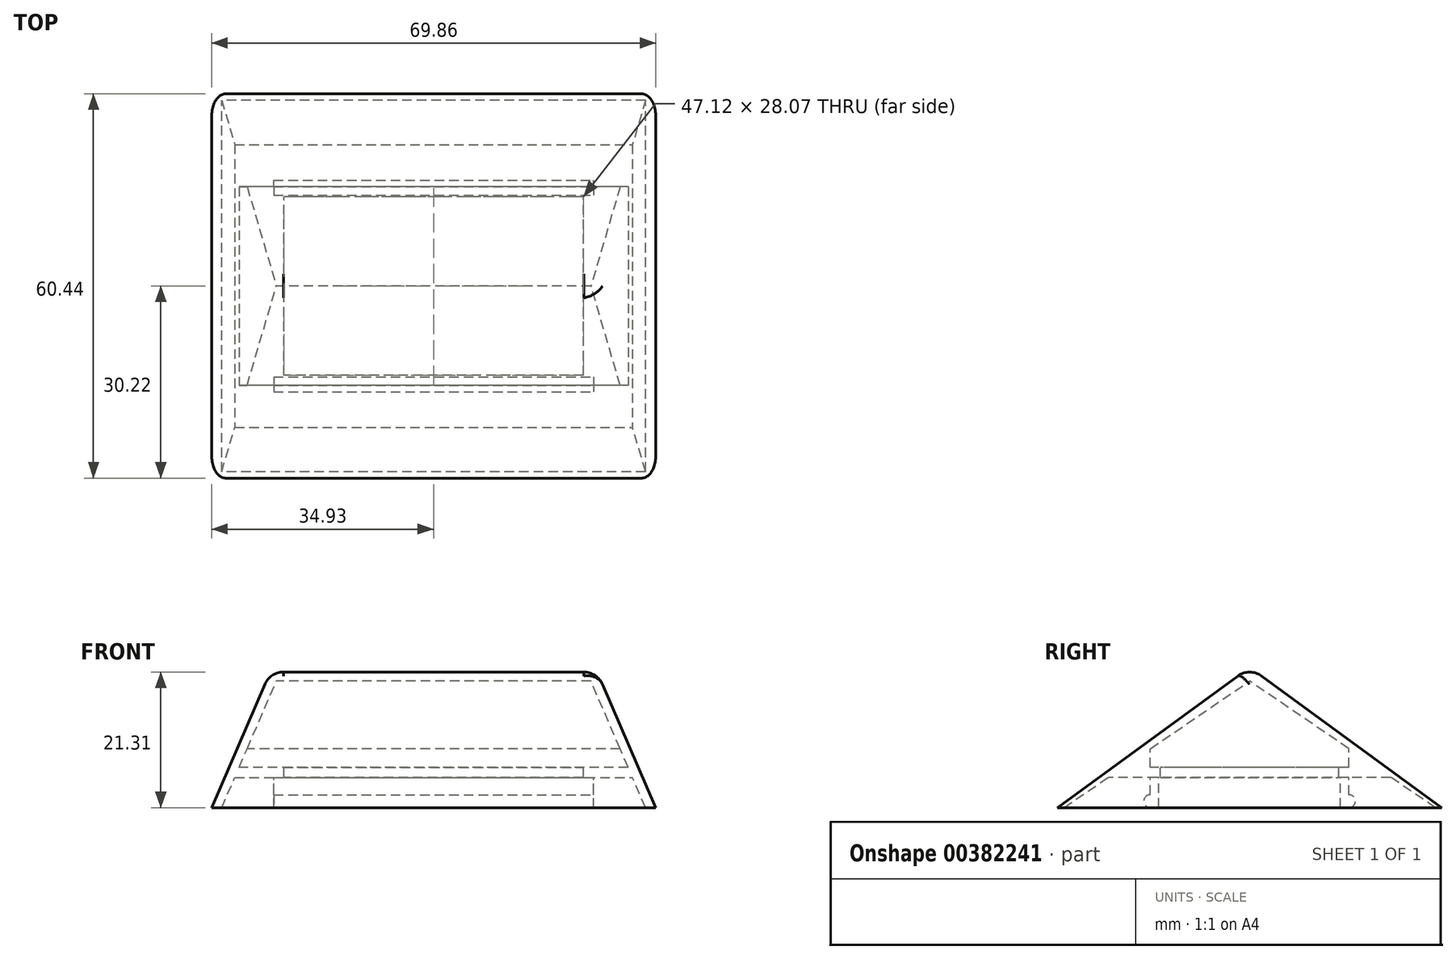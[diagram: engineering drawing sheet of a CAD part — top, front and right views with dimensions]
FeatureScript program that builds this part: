
annotation { "Feature Type Name" : "Feature", "Feature Type Description" : "" }
export const myFeature = defineFeature(function(context is Context, id is Id, definition is map)
    precondition{}
    {
        {
            var Q0;
            Q0=qCreatedBy(makeId("Top.planeOp"),FACE);
            var sketch = newSketch(context, id + "F0", { "sketchPlane" : qUnion([Q0])});
            skLineSegment(sketch, "E0.bottom", {"start": v(-31.75, 22.22) * mm, "end": v(31.75, 22.22) * mm});
            skLineSegment(sketch, "E0.top", {"start": v(-31.75, -22.22) * mm, "end": v(31.75, -22.22) * mm});
            skLineSegment(sketch, "E0.left", {"start": v(-31.75, 22.23) * mm, "end": v(-31.75, -22.22) * mm});
            skLineSegment(sketch, "E0.right", {"start": v(31.75, 22.23) * mm, "end": v(31.75, -22.22) * mm});
            skLineSegment(sketch, "E1.0", {"start": v(-25.15, 15.62) * mm, "end": v(25.15, 15.62) * mm});
            skLineSegment(sketch, "E1.1", {"start": v(-25.15, 15.62) * mm, "end": v(-25.15, -15.62) * mm});
            skLineSegment(sketch, "E1.2", {"start": v(-25.15, -15.62) * mm, "end": v(25.15, -15.62) * mm});
            skLineSegment(sketch, "E1.3", {"start": v(25.15, 15.62) * mm, "end": v(25.15, -15.62) * mm});
            skLineSegment(sketch, "E2", {"start": v(-25.15, 15.62) * mm, "end": v(25.15, -15.62) * mm, "construction": true});
            skLineSegment(sketch, "E3", {"start": v(25.15, 15.62) * mm, "end": v(-25.15, -15.62) * mm, "construction": true});
            skSolve(sketch);
        }
        {
            var Q0;
            Q0 = qSketchRegion(id + "F0", true);
            extrude(context, id + "F1", {"entities" : qUnion([Q0]), "depth" : 1.59 * mm});
        }
        {
            var Q0;
            Q0=makeQuery(id+"F1.opExtrude","CAP_FACE",FACE,{"disambiguationData":[OSD([sQuery(id+"F0.wireOp",EDGE,"E0.bottom"),sQuery(id+"F0.wireOp",EDGE,"E0.top"),sQuery(id+"F0.wireOp",EDGE,"E0.left"),sQuery(id+"F0.wireOp",EDGE,"E0.right"),sQuery(id+"F0.wireOp",EDGE,"E1.0"),sQuery(id+"F0.wireOp",EDGE,"E1.1"),sQuery(id+"F0.wireOp",EDGE,"E1.2"),sQuery(id+"F0.wireOp",EDGE,"E1.3")])],"isStart":false});
            var sketch = newSketch(context, id + "F2", { "sketchPlane" : qUnion([Q0])});
            skLineSegment(sketch, "E4.bottom", {"start": v(-25.15, 15.62) * mm, "end": v(25.15, 15.62) * mm});
            skLineSegment(sketch, "E4.top", {"start": v(-25.15, -15.62) * mm, "end": v(25.15, -15.62) * mm});
            skLineSegment(sketch, "E4.left", {"start": v(-25.15, 15.62) * mm, "end": v(-25.15, -15.62) * mm});
            skLineSegment(sketch, "E4.right", {"start": v(25.15, 15.62) * mm, "end": v(25.15, -15.62) * mm});
            skLineSegment(sketch, "E5.0", {"start": v(-23.56, 14.03) * mm, "end": v(23.56, 14.03) * mm});
            skLineSegment(sketch, "E5.1", {"start": v(-23.56, 14.03) * mm, "end": v(-23.56, -14.03) * mm});
            skLineSegment(sketch, "E5.2", {"start": v(-23.56, -14.03) * mm, "end": v(23.56, -14.03) * mm});
            skLineSegment(sketch, "E5.3", {"start": v(23.56, 14.03) * mm, "end": v(23.56, -14.03) * mm});
            skSolve(sketch);
        }
        {
            var Q0;
            Q0 = qSketchRegion(id + "F2", true);
            extrude(context, id + "F3", {"entities" : qUnion([Q0]), "operationType" : NewBodyOperationType.ADD, "oppositeDirection" : true, "depth" : 6.35 * mm});
        }
        {
            var Q0;
            Q0=qCreatedBy(makeId("Right.planeOp"),FACE);
            var sketch = newSketch(context, id + "F4", { "sketchPlane" : qUnion([Q0])});
            skLineSegment(sketch, "E6", {"start": v(0, 15.15) * mm, "end": v(15.61, 4.5) * mm});
            skLineSegment(sketch, "E7", {"start": v(29.21, -4.76) * mm, "end": v(32.39, -4.76) * mm});
            skLineSegment(sketch, "E8", {"start": v(32.39, -4.76) * mm, "end": v(0, 17.3) * mm});
            skLineSegment(sketch, "E9", {"start": v(15.61, 4.5) * mm, "end": v(15.61, 0) * mm});
            skLineSegment(sketch, "E10", {"start": v(15.61, 0) * mm, "end": v(22.23, 0) * mm});
            skLineSegment(sketch, "E11.trimOffspring", {"start": v(22.23, 0) * mm, "end": v(29.21, -4.76) * mm});
            skLineSegment(sketch, "E12.MirrorCS", {"start": v(0, 15.15) * mm, "end": v(-15.61, 4.5) * mm});
            skLineSegment(sketch, "E13.MirrorCS", {"start": v(-32.39, -4.76) * mm, "end": v(0, 17.3) * mm});
            skLineSegment(sketch, "E14.MirrorCS", {"start": v(-15.61, 4.5) * mm, "end": v(-15.61, 0) * mm});
            skLineSegment(sketch, "E15.MirrorCS", {"start": v(-29.21, -4.76) * mm, "end": v(-32.39, -4.76) * mm});
            skLineSegment(sketch, "E16.MirrorCS", {"start": v(-15.61, 0) * mm, "end": v(-22.23, 0) * mm});
            skLineSegment(sketch, "E17.MirrorCS", {"start": v(-22.23, 0) * mm, "end": v(-29.21, -4.76) * mm});
            skSolve(sketch);
        }
        {
            var Q0;
            Q0 = qSketchRegion(id + "F4", true);
            extrude(context, id + "F5", {"entities" : qUnion([Q0]), "operationType" : NewBodyOperationType.ADD, "endBound" : BoundingType.SYMMETRIC, "depth" : 69.85 * mm});
        }
        {
            var Q0;
            Q0=qCreatedBy(makeId("Front.planeOp"),FACE);
            var sketch = newSketch(context, id + "F6", { "sketchPlane" : qUnion([Q0])});
            skLineSegment(sketch, "E18", {"start": v(-25.4, 17.3) * mm, "end": v(-34.93, -4.76) * mm});
            skLineSegment(sketch, "E19", {"start": v(-25.4, 17.3) * mm, "end": v(-34.93, 17.3) * mm});
            skLineSegment(sketch, "E20", {"start": v(-34.93, 17.3) * mm, "end": v(-34.93, -4.76) * mm});
            skLineSegment(sketch, "E21.MirrorCS", {"start": v(34.93, 17.3) * mm, "end": v(34.93, -4.76) * mm});
            skLineSegment(sketch, "E22.MirrorCS", {"start": v(25.4, 17.3) * mm, "end": v(34.93, 17.3) * mm});
            skLineSegment(sketch, "E23.MirrorCS", {"start": v(25.4, 17.3) * mm, "end": v(34.93, -4.76) * mm});
            skSolve(sketch);
        }
        {
            var Q0;
            Q0 = qSketchRegion(id + "F6", true);
            extrude(context, id + "F7", {"entities" : qUnion([Q0]), "operationType" : NewBodyOperationType.REMOVE, "endBound" : BoundingType.SYMMETRIC, "oppositeDirection" : true, "depth" : 76.2 * mm});
        }
        {
            var Q0;
            Q0=qCreatedBy(makeId("Front.planeOp"),FACE);
            var sketch = newSketch(context, id + "F8", { "sketchPlane" : qUnion([Q0])});
            skLineSegment(sketch, "E24", {"start": v(-25.4, 17.3) * mm, "end": v(-34.93, -4.76) * mm});
            skLineSegment(sketch, "E25", {"start": v(-34.93, -4.76) * mm, "end": v(-33.34, -4.76) * mm});
            skLineSegment(sketch, "E26", {"start": v(-33.34, -4.76) * mm, "end": v(-23.81, 17.3) * mm});
            skLineSegment(sketch, "E27", {"start": v(-23.81, 17.3) * mm, "end": v(-25.4, 17.3) * mm});
            skLineSegment(sketch, "E28.MirrorCS", {"start": v(25.4, 17.3) * mm, "end": v(34.93, -4.76) * mm});
            skLineSegment(sketch, "E29.MirrorCS", {"start": v(23.81, 17.3) * mm, "end": v(25.4, 17.3) * mm});
            skLineSegment(sketch, "E30.MirrorCS", {"start": v(34.93, -4.76) * mm, "end": v(33.34, -4.76) * mm});
            skLineSegment(sketch, "E31.MirrorCS", {"start": v(33.34, -4.76) * mm, "end": v(23.81, 17.3) * mm});
            skSolve(sketch);
        }
        {
            var Q0;
            Q0 = qSketchRegion(id + "F8", true);
            extrude(context, id + "F9", {"entities" : qUnion([Q0]), "operationType" : NewBodyOperationType.ADD, "endBound" : BoundingType.SYMMETRIC, "depth" : 76.2 * mm});
        }
        {
            var Q0;
            Q0=qCreatedBy(makeId("Right.planeOp"),FACE);
            var sketch = newSketch(context, id + "F10", { "sketchPlane" : qUnion([Q0])});
            skLineSegment(sketch, "E32", {"start": v(0, 17.3) * mm, "end": v(-30.22, -4.76) * mm});
            skLineSegment(sketch, "E33", {"start": v(-30.22, -4.76) * mm, "end": v(-38.1, -4.76) * mm});
            skLineSegment(sketch, "E34", {"start": v(-38.1, -4.76) * mm, "end": v(-38.1, 17.3) * mm});
            skLineSegment(sketch, "E35", {"start": v(-38.1, 17.3) * mm, "end": v(0, 17.3) * mm});
            skLineSegment(sketch, "E36.MirrorCS", {"start": v(0, 17.3) * mm, "end": v(30.22, -4.76) * mm});
            skLineSegment(sketch, "E37.MirrorCS", {"start": v(30.22, -4.76) * mm, "end": v(38.1, -4.76) * mm});
            skLineSegment(sketch, "E38.MirrorCS", {"start": v(38.1, -4.76) * mm, "end": v(38.1, 17.3) * mm});
            skLineSegment(sketch, "E39.MirrorCS", {"start": v(38.1, 17.3) * mm, "end": v(0, 17.3) * mm});
            skSolve(sketch);
        }
        {
            var Q0;
            Q0 = qSketchRegion(id + "F10", true);
            extrude(context, id + "F11", {"entities" : qUnion([Q0]), "operationType" : NewBodyOperationType.REMOVE, "endBound" : BoundingType.SYMMETRIC, "oppositeDirection" : true, "depth" : 76.2 * mm});
        }
        {
            var Q0;
            Q0=makeQuery(id+"F11.boolean.opBoolean","INTERSECT",EDGE,{"derivedFrom":[makeQuery(id+"F9.boolean.opBoolean","MERGE",FACE,{"derivedFrom":[makeQuery(id+"F7.boolean.opBoolean","COPY",FACE,{"derivedFrom":makeQuery(id+"F7.opExtrude","SWEPT_FACE",FACE,{"disambiguationData":[OSD([sQuery(id+"F6.wireOp",EDGE,"E23.MirrorCS")])]})}),makeQuery(id+"F9.opExtrude","SWEPT_FACE",FACE,{"disambiguationData":[OSD([sQuery(id+"F8.wireOp",EDGE,"E28.MirrorCS")])]})]}),makeQuery(id+"F11.opExtrude","SWEPT_FACE",FACE,{"disambiguationData":[OSD([sQuery(id+"F10.wireOp",EDGE,"E32")])]})]});
            var Q1;
            Q1=makeQuery(id+"F11.boolean.opBoolean","INTERSECT",EDGE,{"derivedFrom":[makeQuery(id+"F9.boolean.opBoolean","MERGE",FACE,{"derivedFrom":[makeQuery(id+"F7.boolean.opBoolean","COPY",FACE,{"derivedFrom":makeQuery(id+"F7.opExtrude","SWEPT_FACE",FACE,{"disambiguationData":[OSD([sQuery(id+"F6.wireOp",EDGE,"E23.MirrorCS")])]})}),makeQuery(id+"F9.opExtrude","SWEPT_FACE",FACE,{"disambiguationData":[OSD([sQuery(id+"F8.wireOp",EDGE,"E28.MirrorCS")])]})]}),makeQuery(id+"F11.opExtrude","SWEPT_FACE",FACE,{"disambiguationData":[OSD([sQuery(id+"F10.wireOp",EDGE,"E36.MirrorCS")])]})]});
            var Q2;
            {var subQ0=sQuery(id+"F10.wireOp",EDGE,"E36.MirrorCS");var subQ1=sQuery(id+"F10.wireOp",EDGE,"E39.MirrorCS");var subQ2=sQuery(id+"F10.wireOp",EDGE,"E35");var subQ3=sQuery(id+"F10.wireOp",EDGE,"E32");Q2=makeQuery(id+"F11.boolean.opBoolean","MERGE",EDGE,{"derivedFrom":[makeQuery(id+"F5.opExtrude","SWEPT_EDGE",EDGE,{"disambiguationData":[OSD([sQuery(id+"F4.wireOp",EDGE,"E8"),sQuery(id+"F4.wireOp",EDGE,"E13.MirrorCS")])]}),makeQuery(id+"F11.opExtrude","SWEPT_EDGE",EDGE,{"disambiguationData":[OSD([subQ3,subQ2,subQ0,subQ1]),ownerDisambiguation([makeQuery(id+"F10.imprint","IMPRINT",EDGE,{"derivedFrom":subQ3})])]}),makeQuery(id+"F11.opExtrude","SWEPT_EDGE",EDGE,{"disambiguationData":[OSD([subQ3,subQ2,subQ0,subQ1]),ownerDisambiguation([makeQuery(id+"F10.imprint","IMPRINT",EDGE,{"derivedFrom":subQ0})])]})]});}
            var Q3;
            Q3=makeQuery(id+"F11.boolean.opBoolean","INTERSECT",EDGE,{"derivedFrom":[makeQuery(id+"F9.boolean.opBoolean","MERGE",FACE,{"derivedFrom":[makeQuery(id+"F7.boolean.opBoolean","COPY",FACE,{"derivedFrom":makeQuery(id+"F7.opExtrude","SWEPT_FACE",FACE,{"disambiguationData":[OSD([sQuery(id+"F6.wireOp",EDGE,"E18")])]})}),makeQuery(id+"F9.opExtrude","SWEPT_FACE",FACE,{"disambiguationData":[OSD([sQuery(id+"F8.wireOp",EDGE,"E24")])]})]}),makeQuery(id+"F11.opExtrude","SWEPT_FACE",FACE,{"disambiguationData":[OSD([sQuery(id+"F10.wireOp",EDGE,"E32")])]})]});
            var Q4;
            Q4=makeQuery(id+"F11.boolean.opBoolean","INTERSECT",EDGE,{"derivedFrom":[makeQuery(id+"F9.boolean.opBoolean","MERGE",FACE,{"derivedFrom":[makeQuery(id+"F7.boolean.opBoolean","COPY",FACE,{"derivedFrom":makeQuery(id+"F7.opExtrude","SWEPT_FACE",FACE,{"disambiguationData":[OSD([sQuery(id+"F6.wireOp",EDGE,"E18")])]})}),makeQuery(id+"F9.opExtrude","SWEPT_FACE",FACE,{"disambiguationData":[OSD([sQuery(id+"F8.wireOp",EDGE,"E24")])]})]}),makeQuery(id+"F11.opExtrude","SWEPT_FACE",FACE,{"disambiguationData":[OSD([sQuery(id+"F10.wireOp",EDGE,"E36.MirrorCS")])]})]});
            fillet(context, id + "F12", {"entities" : qUnion([Q0, Q1, Q2, Q3, Q4]), "radius" : 3.17 * mm, "tangentPropagation" : true, "allowEdgeOverflow" : false});
        }
        {
            var Q0;
            Q0=makeQuery(id+"F3.opExtrude","SWEPT_FACE",FACE,{"disambiguationData":[OSD([sQuery(id+"F2.wireOp",EDGE,"E4.right")])]});
            var sketch = newSketch(context, id + "F13", { "sketchPlane" : qUnion([Q0])});
            skArc(sketch, "E40", {"start": v(-15.62, -2.73) * mm, "mid": v(-16.64, -3.75) * mm, "end": v(-15.62, -4.76) * mm});
            skArc(sketch, "E41.MirrorCS", {"start": v(15.62, -2.73) * mm, "mid": v(16.64, -3.75) * mm, "end": v(15.62, -4.76) * mm});
            skLineSegment(sketch, "E42", {"start": v(-15.62, -2.73) * mm, "end": v(-15.62, -4.76) * mm});
            skLineSegment(sketch, "E43", {"start": v(15.62, -2.73) * mm, "end": v(15.62, -4.76) * mm});
            skSolve(sketch);
        }
        {
            var Q0;
            Q0 = qSketchRegion(id + "F13", true);
            var Q1;
            Q1=makeQuery(id+"F3.opExtrude","SWEPT_FACE",FACE,{"disambiguationData":[OSD([sQuery(id+"F2.wireOp",EDGE,"E4.left")])]});
            extrude(context, id + "F14", {"entities" : qUnion([Q0]), "operationType" : NewBodyOperationType.ADD, "endBound" : BoundingType.UP_TO_SURFACE, "oppositeDirection" : true, "endBoundEntityFace" : qUnion([Q1]), "depth" : 25.4 * mm});
        }
        {
            var Q0;
            Q0=makeQuery(id+"F14.boolean.opBoolean","MERGE",FACE,{"derivedFrom":[makeQuery(id+"F3.opExtrude","SWEPT_FACE",FACE,{"disambiguationData":[OSD([sQuery(id+"F2.wireOp",EDGE,"E4.right")])]}),makeQuery(id+"F14.opExtrude","CAP_FACE",FACE,{"disambiguationData":[OSD([sQuery(id+"F13.wireOp",EDGE,"E40"),sQuery(id+"F13.wireOp",EDGE,"E42")])],"isStart":true}),makeQuery(id+"F14.opExtrude","CAP_FACE",FACE,{"disambiguationData":[OSD([sQuery(id+"F13.wireOp",EDGE,"E41.MirrorCS"),sQuery(id+"F13.wireOp",EDGE,"E43")])],"isStart":true})]});
            var sketch = newSketch(context, id + "F15", { "sketchPlane" : qUnion([Q0])});
            skLineSegment(sketch, "E44.bottom", {"start": v(-14.29, -4.76) * mm, "end": v(14.29, -4.76) * mm});
            skLineSegment(sketch, "E44.top", {"start": v(-14.29, 0) * mm, "end": v(14.29, 0) * mm});
            skLineSegment(sketch, "E44.left", {"start": v(-14.29, -4.76) * mm, "end": v(-14.29, 0) * mm});
            skLineSegment(sketch, "E44.right", {"start": v(14.29, -4.76) * mm, "end": v(14.29, 0) * mm});
            skLineSegment(sketch, "E45", {"start": v(15.62, -1.37) * mm, "end": v(-15.62, -1.37) * mm, "construction": true});
            skLineSegment(sketch, "E46", {"start": v(0, -1.37) * mm, "end": v(0, 0) * mm, "construction": true});
            skSolve(sketch);
        }
        {
            var Q0;
            Q0 = qSketchRegion(id + "F15", true);
            var Q1;
            {var subQ0=sQuery(id+"F2.wireOp",EDGE,"E4.left");Q1=makeQuery(id+"F14.boolean.opBoolean","MERGE",FACE,{"derivedFrom":[makeQuery(id+"F3.opExtrude","SWEPT_FACE",FACE,{"disambiguationData":[OSD([subQ0])]}),makeQuery(id+"F14.opExtrude","CAP_FACE",FACE,{"disambiguationData":[OSD([subQ0]),ownerDisambiguation([makeQuery(id+"F13.imprint","IMPRINT",EDGE,{"derivedFrom":sQuery(id+"F13.wireOp",EDGE,"E40")})])],"isStart":false}),makeQuery(id+"F14.opExtrude","CAP_FACE",FACE,{"disambiguationData":[OSD([subQ0]),ownerDisambiguation([makeQuery(id+"F13.imprint","IMPRINT",EDGE,{"derivedFrom":sQuery(id+"F13.wireOp",EDGE,"E41.MirrorCS")})])],"isStart":false})]});}
            extrude(context, id + "F16", {"entities" : qUnion([Q0]), "operationType" : NewBodyOperationType.REMOVE, "endBound" : BoundingType.UP_TO_SURFACE, "oppositeDirection" : true, "endBoundEntityFace" : qUnion([Q1]), "depth" : 25.4 * mm});
        }
    });
